# Revit family: Digidim 250mA Dali Power Supply_402
name_source: partatom
category: Electrical Fixtures
revit_build: Autodesk Revit 2018 (Build: 20170223_1515(x64)
units: mm (PartAtom-declared; Revit-internal decimal feet)

## family parameters
Always vertical = Yes
Cut with Voids When Loaded = No
Maintain Annotation Orientation = No
OmniClass Number = 23.80.00.00
OmniClass Title = Electric Power and Lighting
Part Type = Normal
Room Calculation Point = No
Round Connector Dimension = Use Diameter
Shared = No
Work Plane-Based = Yes

## types (1)
- DIGIDIM 250mA DALI POWER SUPPLY
    Ambient temperature = 0 °C to + 40 °C
    DALI consumption = None
    DALI: = Standard DIGIDIM terminal
block 0.5 mm² – 1.5 mm² solid
or stranded
    Dali supply = 20 VDC (nominal), 250 mA
    Default Elevation = 0 mm  [stored 0 ft]
    Dimensions: = 35 mm × 90 mm × 58 mm
    EMC emission = EN 61000-6-3
    EMC immunity = EN 61547
    External protection = 6 A MCB maximum. The
external mains supply to the
unit must be protected
    Housing = DIN rail case 35 mm wide
    IP code: = IP30
    Isolation = 3 kV
    Mains Supply = 100 VAC – 240 VAC (nominal)
85 VAC – 264 VAC (absolute)
45 Hz – 65 Hz
    Mains: = Up to 4 mm² solid, or up
to 2.5 mm² stranded
    Manufacturer = Helvar
    Model = 402
    Relative humidity = Max. 90 %, noncondensing
    Safety = EN 60950
    Storage temperature = −10 °C to + 70 °C
    Weight: = 80 g

note: [stored X ft] marks values corroborated as IEEE doubles in the binary element streams (Revit-internal decimal feet)

## geometry (parser evidence)
native form markers: Sweep x3
no freeform markers — native parametric forms only
